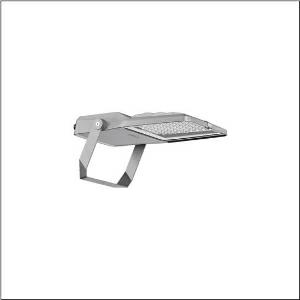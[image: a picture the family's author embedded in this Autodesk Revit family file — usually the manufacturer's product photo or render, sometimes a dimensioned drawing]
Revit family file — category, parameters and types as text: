
# Revit family: floodlight_fl_21_mini___rs12_5xa7772c1b1a_b8a2
name_source: partatom
category: Lighting Fixtures
units: mm (PartAtom-declared; Revit-internal decimal feet)

## family parameters
Cut with Voids When Loaded = No
Host = Face
Light Source = No
Part Type = Normal
Room Calculation Point = No
Round Connector Dimension = Use Diameter
Shared = No

## types (1)
- --- (1 x LED, 10220 lm, 87.2 W, 2200K)
    Apparent Load = 87 VA
    CIE Flux Codes = 79 92 99 100 100
    Color Rendering = 70
    Color Temperature = 2200K
    Default Elevation = 1800 mm
    Description = Floodlight FL 21 mini, floodlight, primary light control with lens, of PMMA, primary optical cover: protective disc, of toughened safety glass, transparent, light distribution: RS12, light emission: direct distribution, installation type: surface-mounted, LED, High Power LED, rated luminous flux: 10.220lm, luminous efficacy: 117lm/W, light colour: 722, colour temperature: 2200K, control gear: ECG iQ, control: Street-Remote, Auto-Match, Temp-Guard, Night-Set, Smart-Wire, Desk-Remote (wireless, voltage-free reading and setting of iQ features in the workshop via application-optimized NFC function/RFID function), optimised constant luminous flux control (CLO 2.0), with terminal, 6-pole, mains connection: 220..240V, AC, 50/60Hz, start of lifetime: 87W, end of lifetime: 92W, reduction: 40W, luminaire housing, of diecast aluminium, powder-coated, Siteco® metallic grey (DB 702S), corrosivity category C5 according to DIN EN ISO 12944, mounting bracket, of steel, galvanised, powder-coated, Siteco® metallic grey (DB 702S), protection rating (complete): IP66, insulation class (complete): insulation class II (safety insulation), certification: CE, ENEC, VDE, protection symbol: D, impact resistance: IK08, permissible operating ambient temperature: -40..+40°C, permissible operating ambient temperature for outdoor applications: -40..+50°C, standard: DIN EN 12944, packaging unit: 1 piece

Light Distribution: RS12
    Height = 70 mm
    Lamp = 1 x LED
    Lamp Light Flux = 10220 lm
    Lamp Power = 87.2 W
    Lamp count = 1
    Length = 485 mm
    Luminous efficacy = 117 lm/W
    Manufacturer = Siteco
    ModVariant = No
    Model = 5XA7772C1B1A
    Number of Poles = 1
    OnlyDefault = Yes
    Power Factor = 1
    Product Name = Floodlight FL 21 mini | RS12
    Product group = floodlight | pylon top
    ProductGroupID = 6101
    Protection Class = Protection class II
    Protection Degree = IP 66
    RLX_Detail_Level = 1
    RlxData = <blob elided: 90653 chars, md5=1df4e638>
    Socket = socket
    Standby Power = 0 W
    System Light Flux = 10220 lm
    System Power = 87 W
    Type Comments = factory setting: luminous flux: 100 % | dim-lin: 254 | 456 mA
    Type Image = l_1006845.jpg
    URL = http://relux.com
    VarID = @adj_078739
    Voltage = 0 V
    Weight = 0.00 kg
    Width = 337 mm

## geometry (parser evidence)
native form markers: Blend x4, Sweep x12
no freeform markers — native parametric forms only
